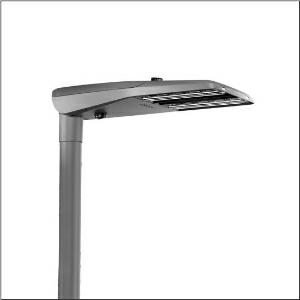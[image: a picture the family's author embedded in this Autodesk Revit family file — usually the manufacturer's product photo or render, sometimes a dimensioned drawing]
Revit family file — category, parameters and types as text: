
# Revit family: streetlight_sl_11_iq_midi___st1_0st0_5_5xc3j51y08me_1f9d
name_source: partatom
category: Lighting Fixtures
units: mm (PartAtom-declared; Revit-internal decimal feet)

## family parameters
Cut with Voids When Loaded = No
Host = Face
Light Source = No
Part Type = Normal
Room Calculation Point = No
Round Connector Dimension = Use Diameter
Shared = No

## types (1)
- --- (1 x LED, 17650 lm, 122.7 W, 3000K)
    Apparent Load = 123 VA
    CIE Flux Codes = 35 68 96 100 100
    Color Rendering = 70
    Color Temperature = 3000K
    Default Elevation = 1800 mm
    Description = Streetlight SL 11 iQ midi, mast luminaire, primary light control with 3 zone facetted reflector, of plastic, silver coated, highly specular, primary optical cover: cover, of PMMA, transparent, light distribution: ST1.0ST0.5, light emission: direct distribution, primary light characteristic: asymmetric, installation type: post-top, side-entry, lamps: LED, High Power LED, rated values: 17.650lm | 122,7W | 143,8lm/W (begin service life); end service life: 17.650lm | 130,2W; at 50% lumin. flux: 8.825lm | 56,1W | 157,3lm/W, colour temperature: 3000K, colour rendering: CRI > 70, light colour: 730, light setting 1 begin service life: 100% | 17.650lm | 122,7W | 143,8lm/W | 3.000K, light setting 1 end service life: 130,2W, further light settings possible, control: pre-setting: logarithmic dimming characteristic, Street-Remote, Auto-Match, Temp-Guard, Lumen-Switch, Night-Set, Smart-Wire, Light-Fading, Desk-Remote (wireless, voltage-free reading and setting of iQ features in the workshop via application-optimized NFC function/RFID function), optimised constant luminous flux control (CLO 2.0), with cable H07RN-F 3x 1.5mm², mains connection: 230..240V, AC, 50/60Hz, connection cable pre-assembled, cable length: 12,5m, luminaire housing, of diecast aluminium, powder-coated, SITECO metallic grey (DB 702S), please order mast flange separately, inclination adjustable without tools: 0°, 5°, 10°, 15° (post-top) | 0°, -5°, -10°, -15° (side-entry), sealing non-destructively replaceable, multi-level sealing system, length: 780mm, width: 376mm, height: 118mm, mast flange for spigot size: 42mm (side-entry): 5XC10008XM4, 60/48mm (side-entry/post-top): 5XC10108XM2, 76/60mm (side-entry/post-top): 5XC10108XM1, equipment: Power, Smart Interface below and above, protection rating (complete): IP66, insulation class (complete): insulation class II (safety insulation), certification: CE, ENEC, ENEC+, VDE, UKCA, impact resistance: IK10, permissible operating ambient temperature for outdoor applications: -25..+50°C, standard-compliant lighting for roads and squares, Environmental Product Declaration (EPD) tested and certified by an independent institute, packaging unit: 1 piece

Light Distribution: ST1.0ST0.5
    Height = 118 mm
    Lamp = 1 x LED
    Lamp Light Flux = 17650 lm
    Lamp Power = 122.7 W
    Lamp count = 1
    Length = 780 mm
    Luminous efficacy = 144 lm/W
    Manufacturer = Siteco
    ModVariant = No
    Model = 5XC3J51Y08ME
    Number of Poles = 1
    OnlyDefault = Yes
    Power Factor = 1
    Product Name = Streetlight SL 11 iQ midi | ST1.0ST0.5
    Product group = mast luminaire | pylon top
    ProductGroupID = 6100
    Protection Class = Protection class II
    Protection Degree = IP 66
    RLX_Detail_Level = 1
    RLX_Emergency_Light_Flux = 0 lm
    RLX_Emergency_Type = 0
    RLX_Emergency_Type_DB = No
    RlxData = <blob elided: 69717 chars, md5=056cadea>
    Socket = socket
    Standby Power = 0 W
    System Light Flux = 17650 lm
    System Power = 123 W
    Type Comments = factory setting: luminous flux: 100 % | dim-lin: 254 | 553 mA
    Type Image = l_1004429.jpg
    URL = http://relux.com
    VarID = @adj_047739
    Voltage = 0 V
    Weight = 0.00 kg
    Width = 376 mm

## geometry (parser evidence)
native form markers: Blend x4, Sweep x8
no freeform markers — native parametric forms only
